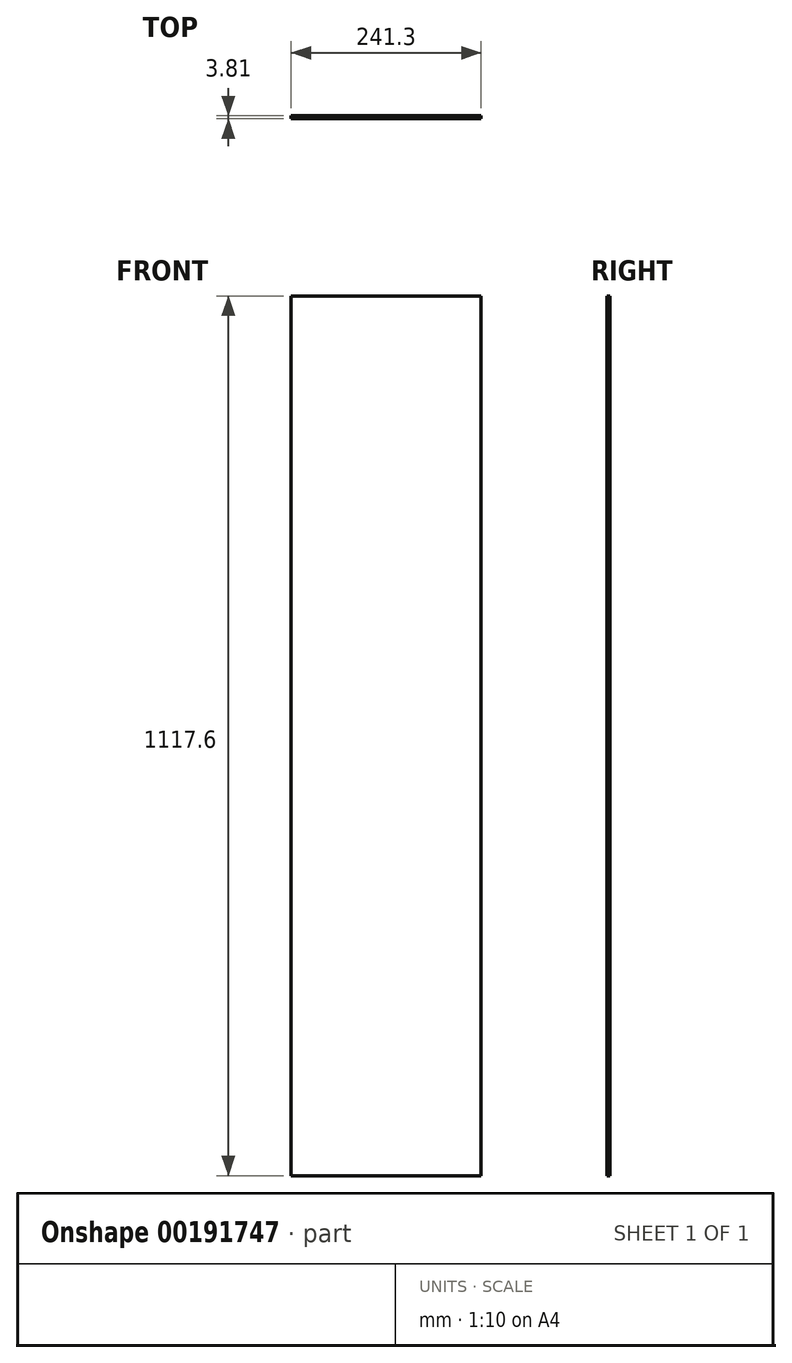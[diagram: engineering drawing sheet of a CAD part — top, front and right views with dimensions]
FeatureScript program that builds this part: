
annotation { "Feature Type Name" : "Feature", "Feature Type Description" : "" }
export const myFeature = defineFeature(function(context is Context, id is Id, definition is map)
    precondition{}
    {
        {
            var Q0;
            Q0=qCreatedBy(makeId("Front.planeOp"),FACE);
            var sketch = newSketch(context, id + "F0", { "sketchPlane" : qUnion([Q0])});
            skLineSegment(sketch, "E0.bottom", {"start": v(-248.8, 558.54) * mm, "end": v(-7.5, 558.54) * mm});
            skLineSegment(sketch, "E0.top", {"start": v(-248.8, -559.06) * mm, "end": v(-7.5, -559.06) * mm});
            skLineSegment(sketch, "E0.left", {"start": v(-248.8, 558.54) * mm, "end": v(-248.8, -559.06) * mm});
            skLineSegment(sketch, "E0.right", {"start": v(-7.5, 558.54) * mm, "end": v(-7.5, -559.06) * mm});
            skSolve(sketch);
        }
        {
            var Q0;
            Q0 = qSketchRegion(id + "F0", true);
            extrude(context, id + "F1", {"entities" : qUnion([Q0]), "depth" : 3.8 * mm});
        }
    });
